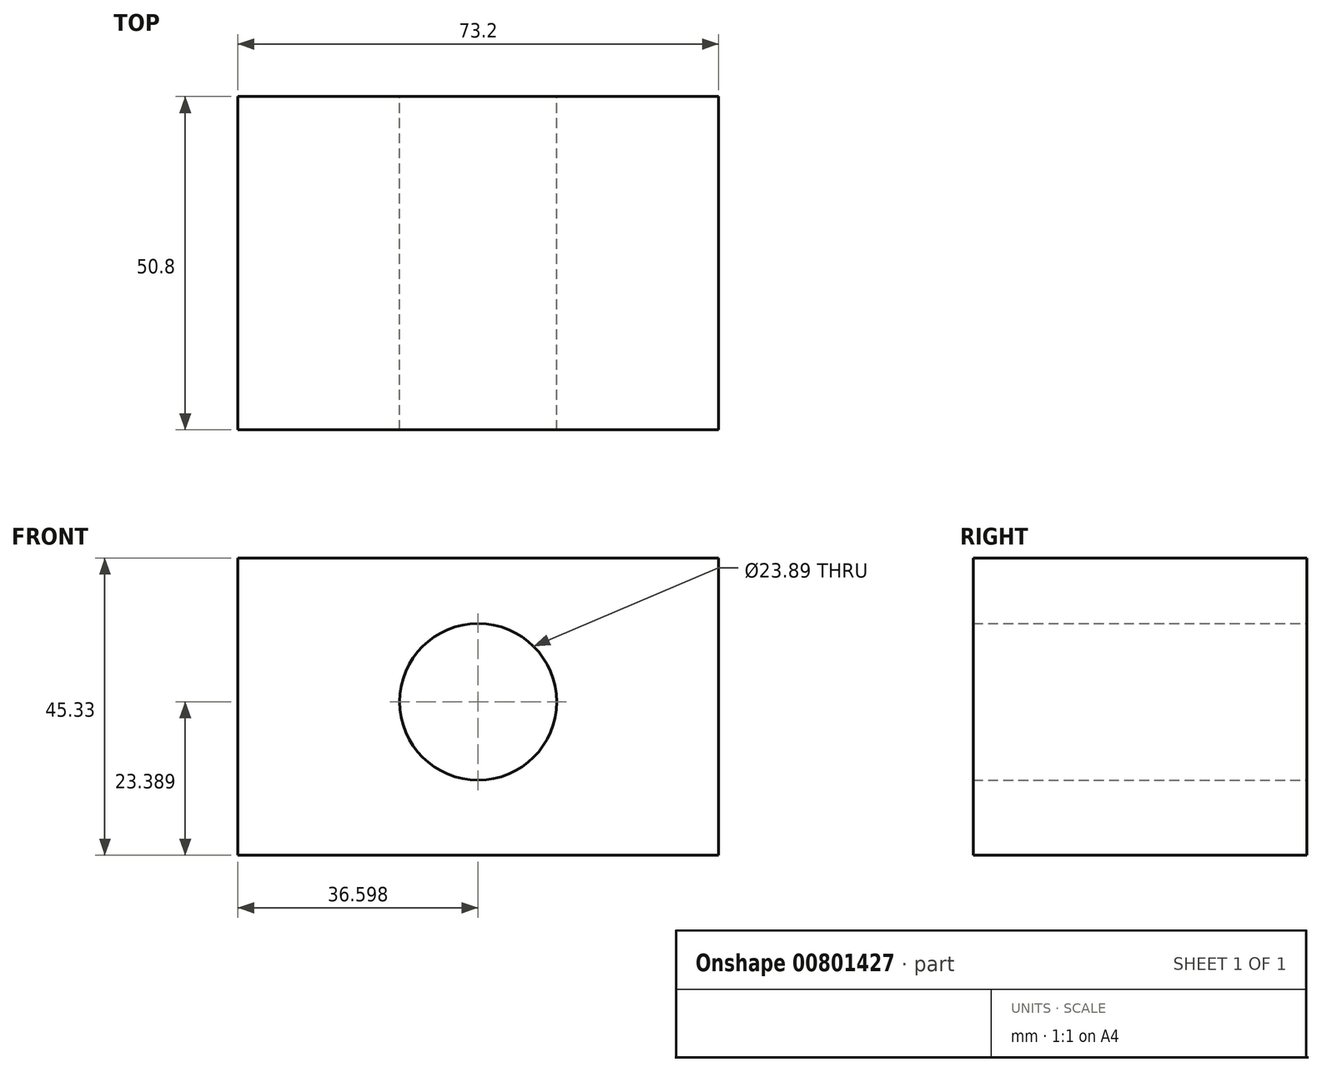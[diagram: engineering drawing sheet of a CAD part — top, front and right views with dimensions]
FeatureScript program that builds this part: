
annotation { "Feature Type Name" : "Feature", "Feature Type Description" : "" }
export const myFeature = defineFeature(function(context is Context, id is Id, definition is map)
    precondition{}
    {
        {
            var Q0;
            Q0=qCreatedBy(makeId("Front.planeOp"),FACE);
            var sketch = newSketch(context, id + "F0", { "sketchPlane" : qUnion([Q0])});
            skLineSegment(sketch, "E0", {"start": v(-54.24, 60.68) * mm, "end": v(18.96, 60.68) * mm});
            skLineSegment(sketch, "E1", {"start": v(18.96, 60.68) * mm, "end": v(18.96, 15.35) * mm});
            skLineSegment(sketch, "E2", {"start": v(18.96, 15.35) * mm, "end": v(-54.24, 15.35) * mm});
            skLineSegment(sketch, "E3", {"start": v(-54.24, 15.35) * mm, "end": v(-54.24, 60.68) * mm});
            skCircle(sketch, "E4", {"center": v(-17.64, 38.74) * mm, "radius": 11.94 * mm});
            skPoint(sketch, "E4.centerSnap0", {"position": v(-17.64, 60.68) * mm});
            skSolve(sketch);
        }
        {
            var Q0;
            Q0 = qSketchRegion(id + "F0", true);
            extrude(context, id + "F1", {"entities" : qUnion([Q0]), "depth" : 50.8 * mm, "offsetDistance" : 25.4 * mm});
        }
    });
